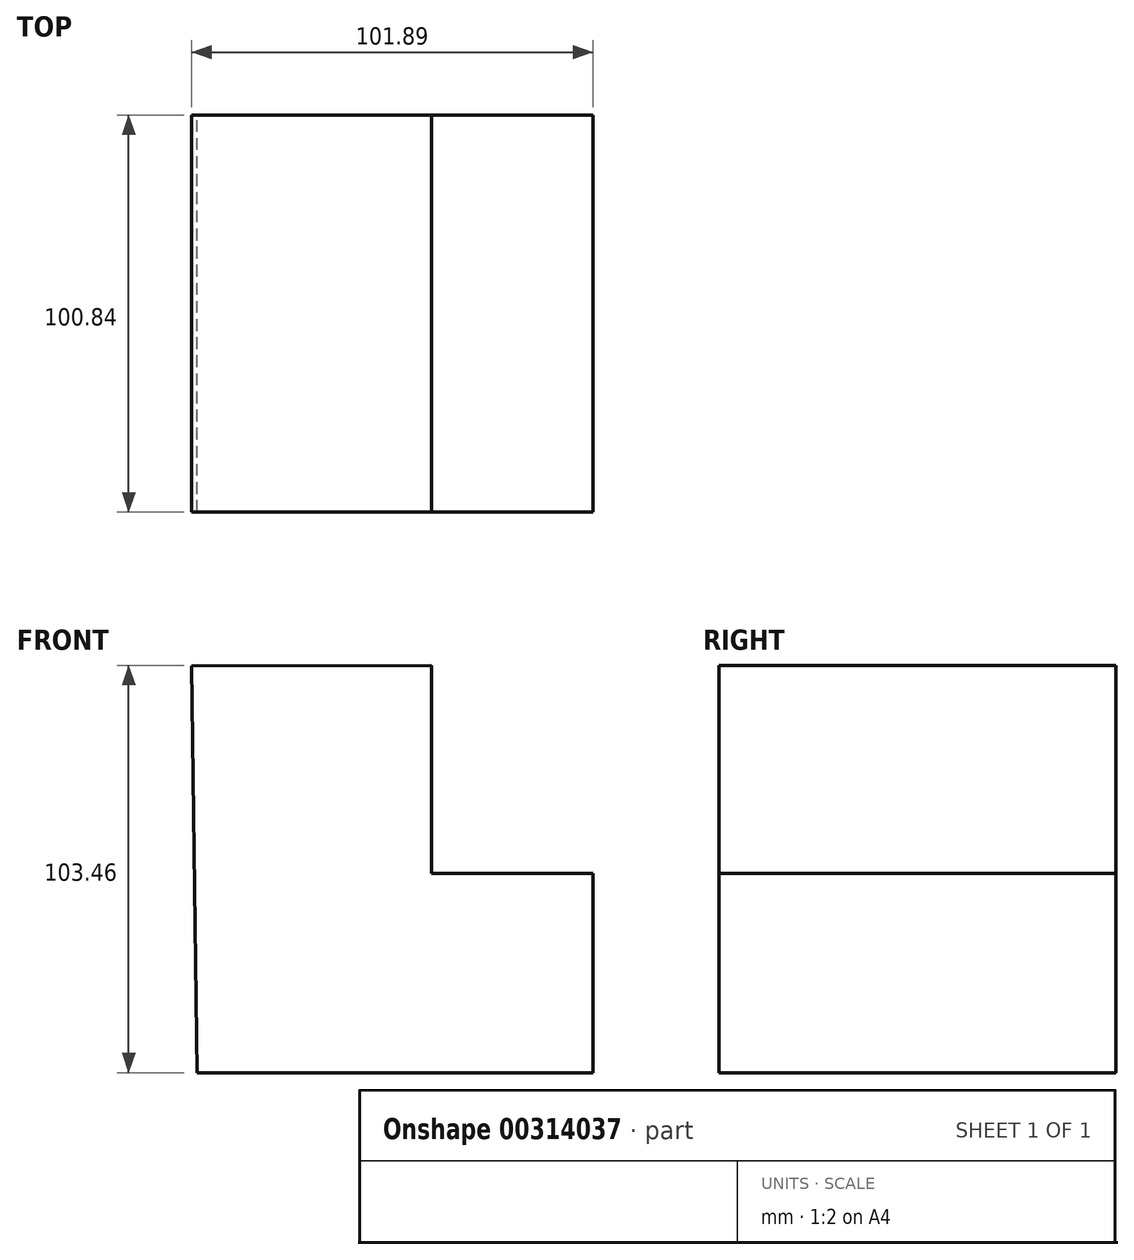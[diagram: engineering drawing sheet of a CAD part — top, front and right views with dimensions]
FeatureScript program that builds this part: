
annotation { "Feature Type Name" : "Feature", "Feature Type Description" : "" }
export const myFeature = defineFeature(function(context is Context, id is Id, definition is map)
    precondition{}
    {
        {
            var Q0;
            Q0=qCreatedBy(makeId("Front.planeOp"),FACE);
            var sketch = newSketch(context, id + "F0", { "sketchPlane" : qUnion([Q0])});
            skLineSegment(sketch, "E0", {"start": v(-39.22, 52.62) * mm, "end": v(-37.84, -50.65) * mm});
            skLineSegment(sketch, "E1", {"start": v(-37.84, -50.65) * mm, "end": v(62.67, -50.65) * mm});
            skLineSegment(sketch, "E2", {"start": v(62.67, -50.65) * mm, "end": v(62.67, 0) * mm});
            skLineSegment(sketch, "E3", {"start": v(62.67, 0) * mm, "end": v(21.68, 0) * mm});
            skLineSegment(sketch, "E4", {"start": v(21.68, 0) * mm, "end": v(21.68, 52.81) * mm});
            skLineSegment(sketch, "E5", {"start": v(21.68, 52.81) * mm, "end": v(-39.22, 52.62) * mm});
            skSolve(sketch);
        }
        {
            var Q0;
            Q0 = qSketchRegion(id + "F0", true);
            extrude(context, id + "F1", {"entities" : qUnion([Q0]), "depth" : 39.37 * mm, "hasSecondDirection" : true, "secondDirectionOppositeDirection" : true, "secondDirectionDepth" : 61.47 * mm});
        }
    });
